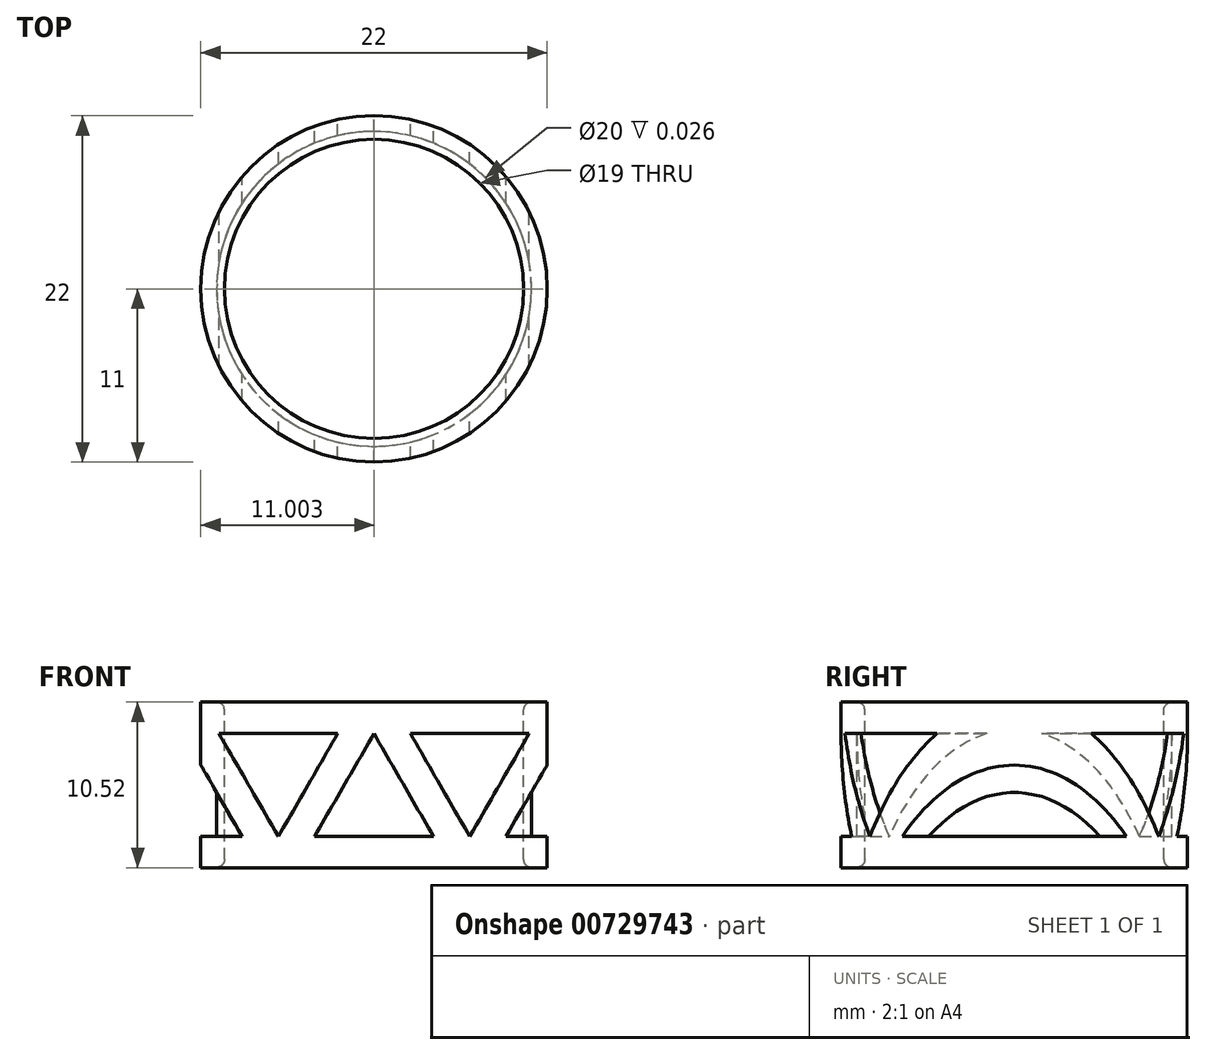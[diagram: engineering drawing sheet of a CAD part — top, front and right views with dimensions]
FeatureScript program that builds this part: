
annotation { "Feature Type Name" : "Feature", "Feature Type Description" : "" }
export const myFeature = defineFeature(function(context is Context, id is Id, definition is map)
    precondition{}
    {
        {
            var Q0;
            Q0=qCreatedBy(makeId("Front.planeOp"),FACE);
            var sketch = newSketch(context, id + "F0", { "sketchPlane" : qUnion([Q0])});
            skLineSegment(sketch, "E0.bottom", {"start": v(-0.17, 7.37) * mm, "end": v(21.83, 7.37) * mm});
            skLineSegment(sketch, "E0.top", {"start": v(-0.17, 17.9) * mm, "end": v(21.83, 17.9) * mm});
            skLineSegment(sketch, "E0.left", {"start": v(-0.17, 7.37) * mm, "end": v(-0.17, 17.9) * mm});
            skLineSegment(sketch, "E0.right", {"start": v(21.83, 7.37) * mm, "end": v(21.83, 17.9) * mm});
            skLineSegment(sketch, "E1", {"start": v(-0.17, 13.9) * mm, "end": v(3.6, 7.37) * mm});
            skLineSegment(sketch, "E2", {"start": v(3.6, 7.37) * mm, "end": v(9.68, 17.9) * mm});
            skLineSegment(sketch, "E3", {"start": v(9.68, 17.9) * mm, "end": v(15.76, 7.37) * mm});
            skLineSegment(sketch, "E4", {"start": v(15.76, 7.37) * mm, "end": v(21.83, 17.9) * mm});
            skLineSegment(sketch, "E5", {"start": v(-0.17, 17.9) * mm, "end": v(5.91, 7.37) * mm});
            skLineSegment(sketch, "E6", {"start": v(5.91, 7.37) * mm, "end": v(11.99, 17.9) * mm});
            skLineSegment(sketch, "E7", {"start": v(11.99, 17.9) * mm, "end": v(18.06, 7.37) * mm});
            skLineSegment(sketch, "E8", {"start": v(18.06, 7.37) * mm, "end": v(21.83, 13.9) * mm});
            skLineSegment(sketch, "E9", {"start": v(-0.17, 15.9) * mm, "end": v(21.83, 15.9) * mm});
            skLineSegment(sketch, "E10", {"start": v(-0.17, 9.37) * mm, "end": v(21.83, 9.37) * mm});
            skSolve(sketch);
        }
        {
            var Q0;
            {var subQ1=sQuery(id+"F0.wireOp",EDGE,"E0.left");var subQ5=sQuery(id+"F0.wireOp",EDGE,"E1");var subQ6=makeQuery(id+"F0.imprint","INTERSECT",VERTEX,{"derivedFrom":[subQ1,subQ5]});Q0=makeQuery(id+"F0.imprint","IMPRINT",FACE,{"disambiguationData":[TD([[makeQuery(id+"F0.imprint","IMPRINT",EDGE,{"disambiguationData":[TD([[subQ6,-1.0]])],"derivedFrom":subQ1}),-1.0]])]});}
            var Q1;
            {var subQ3=sQuery(id+"F0.wireOp",EDGE,"E2");var subQ5=sQuery(id+"F0.wireOp",EDGE,"E9");var subQ6=makeQuery(id+"F0.imprint","INTERSECT",VERTEX,{"derivedFrom":[subQ3,subQ5]});Q1=makeQuery(id+"F0.imprint","IMPRINT",FACE,{"disambiguationData":[TD([[makeQuery(id+"F0.imprint","IMPRINT",EDGE,{"disambiguationData":[TD([[subQ6,1.0]])],"derivedFrom":subQ5}),1.0]])]});}
            var Q2;
            {var subQ1=sQuery(id+"F0.wireOp",EDGE,"E2");var subQ3=sQuery(id+"F0.wireOp",EDGE,"E9");var subQ4=makeQuery(id+"F0.imprint","INTERSECT",VERTEX,{"derivedFrom":[subQ1,subQ3]});Q2=makeQuery(id+"F0.imprint","IMPRINT",FACE,{"disambiguationData":[TD([[makeQuery(id+"F0.imprint","IMPRINT",EDGE,{"disambiguationData":[TD([[subQ4,-1.0]])],"derivedFrom":subQ1}),-1.0]])]});}
            var Q3;
            {var subQ0=sQuery(id+"F0.wireOp",EDGE,"E3");var subQ1=sQuery(id+"F0.wireOp",EDGE,"E0.top");var subQ2=makeQuery(id+"F0.imprint","INTERSECT",VERTEX,{"derivedFrom":[subQ1,sQuery(id+"F0.wireOp",EDGE,"E2"),subQ0]});Q3=makeQuery(id+"F0.imprint","IMPRINT",FACE,{"disambiguationData":[TD([[makeQuery(id+"F0.imprint","IMPRINT",EDGE,{"disambiguationData":[TD([[subQ2,-1.0]])],"derivedFrom":subQ1}),-1.0]])]});}
            var Q4;
            {var subQ0=sQuery(id+"F0.wireOp",EDGE,"E7");var subQ3=sQuery(id+"F0.wireOp",EDGE,"E9");var subQ5=makeQuery(id+"F0.imprint","INTERSECT",VERTEX,{"derivedFrom":[subQ0,subQ3]});Q4=makeQuery(id+"F0.imprint","IMPRINT",FACE,{"disambiguationData":[TD([[makeQuery(id+"F0.imprint","IMPRINT",EDGE,{"disambiguationData":[TD([[subQ5,1.0]])],"derivedFrom":subQ0}),-1.0]])]});}
            var Q5;
            {var subQ1=sQuery(id+"F0.wireOp",EDGE,"E0.left");var subQ3=sQuery(id+"F0.wireOp",EDGE,"E9");var subQ4=makeQuery(id+"F0.imprint","INTERSECT",VERTEX,{"derivedFrom":[subQ1,subQ3]});Q5=makeQuery(id+"F0.imprint","IMPRINT",FACE,{"disambiguationData":[TD([[makeQuery(id+"F0.imprint","IMPRINT",EDGE,{"disambiguationData":[TD([[subQ4,-1.0]])],"derivedFrom":subQ3}),1.0]])]});}
            var Q6;
            {var subQ0=sQuery(id+"F0.wireOp",EDGE,"E4");var subQ5=sQuery(id+"F0.wireOp",EDGE,"E9");var subQ6=makeQuery(id+"F0.imprint","INTERSECT",VERTEX,{"derivedFrom":[subQ0,subQ5]});Q6=makeQuery(id+"F0.imprint","IMPRINT",FACE,{"disambiguationData":[TD([[makeQuery(id+"F0.imprint","IMPRINT",EDGE,{"disambiguationData":[TD([[subQ6,1.0]])],"derivedFrom":subQ5}),1.0]])]});}
            var Q7;
            {var subQ1=sQuery(id+"F0.wireOp",EDGE,"E0.right");var subQ3=sQuery(id+"F0.wireOp",EDGE,"E9");var subQ4=makeQuery(id+"F0.imprint","INTERSECT",VERTEX,{"derivedFrom":[subQ1,subQ3]});Q7=makeQuery(id+"F0.imprint","IMPRINT",FACE,{"disambiguationData":[TD([[makeQuery(id+"F0.imprint","IMPRINT",EDGE,{"disambiguationData":[TD([[subQ4,1.0]])],"derivedFrom":subQ3}),1.0]])]});}
            var Q8;
            {var subQ1=sQuery(id+"F0.wireOp",EDGE,"E0.right");var subQ5=sQuery(id+"F0.wireOp",EDGE,"E8");var subQ6=makeQuery(id+"F0.imprint","INTERSECT",VERTEX,{"derivedFrom":[subQ1,subQ5]});Q8=makeQuery(id+"F0.imprint","IMPRINT",FACE,{"disambiguationData":[TD([[makeQuery(id+"F0.imprint","IMPRINT",EDGE,{"disambiguationData":[TD([[subQ6,-1.0]])],"derivedFrom":subQ1}),1.0]])]});}
            var Q9;
            {var subQ0=sQuery(id+"F0.wireOp",EDGE,"E10");var subQ1=sQuery(id+"F0.wireOp",EDGE,"E3");var subQ2=makeQuery(id+"F0.imprint","INTERSECT",VERTEX,{"derivedFrom":[subQ1,subQ0]});Q9=makeQuery(id+"F0.imprint","IMPRINT",FACE,{"disambiguationData":[TD([[makeQuery(id+"F0.imprint","IMPRINT",EDGE,{"disambiguationData":[TD([[subQ2,1.0]])],"derivedFrom":subQ1}),1.0]])]});}
            var Q10;
            {var subQ0=sQuery(id+"F0.wireOp",EDGE,"E9");var subQ1=sQuery(id+"F0.wireOp",EDGE,"E2");var subQ2=makeQuery(id+"F0.imprint","INTERSECT",VERTEX,{"derivedFrom":[subQ1,subQ0]});Q10=makeQuery(id+"F0.imprint","IMPRINT",FACE,{"disambiguationData":[TD([[makeQuery(id+"F0.imprint","IMPRINT",EDGE,{"disambiguationData":[TD([[subQ2,1.0]])],"derivedFrom":subQ1}),-1.0]])]});}
            var Q11;
            {var subQ0=sQuery(id+"F0.wireOp",EDGE,"E2");var subQ1=sQuery(id+"F0.wireOp",EDGE,"E0.bottom");var subQ2=makeQuery(id+"F0.imprint","INTERSECT",VERTEX,{"derivedFrom":[subQ1,sQuery(id+"F0.wireOp",EDGE,"E1"),subQ0]});Q11=makeQuery(id+"F0.imprint","IMPRINT",FACE,{"disambiguationData":[TD([[makeQuery(id+"F0.imprint","IMPRINT",EDGE,{"disambiguationData":[TD([[subQ2,-1.0]])],"derivedFrom":subQ1}),1.0]])]});}
            var Q12;
            {var subQ1=sQuery(id+"F0.wireOp",EDGE,"E1");var subQ3=sQuery(id+"F0.wireOp",EDGE,"E10");var subQ4=makeQuery(id+"F0.imprint","INTERSECT",VERTEX,{"derivedFrom":[subQ1,subQ3]});Q12=makeQuery(id+"F0.imprint","IMPRINT",FACE,{"disambiguationData":[TD([[makeQuery(id+"F0.imprint","IMPRINT",EDGE,{"disambiguationData":[TD([[subQ4,-1.0]])],"derivedFrom":subQ1}),1.0]])]});}
            var Q13;
            {var subQ0=sQuery(id+"F0.wireOp",EDGE,"E0.left");var subQ1=sQuery(id+"F0.wireOp",EDGE,"E0.bottom");var subQ2=makeQuery(id+"F0.imprint","INTERSECT",VERTEX,{"derivedFrom":[subQ1,subQ0]});Q13=makeQuery(id+"F0.imprint","IMPRINT",FACE,{"disambiguationData":[TD([[makeQuery(id+"F0.imprint","IMPRINT",EDGE,{"disambiguationData":[TD([[subQ2,-1.0]])],"derivedFrom":subQ0}),-1.0]])]});}
            var Q14;
            {var subQ0=sQuery(id+"F0.wireOp",EDGE,"E6");var subQ3=sQuery(id+"F0.wireOp",EDGE,"E10");var subQ5=makeQuery(id+"F0.imprint","INTERSECT",VERTEX,{"derivedFrom":[subQ0,subQ3]});Q14=makeQuery(id+"F0.imprint","IMPRINT",FACE,{"disambiguationData":[TD([[makeQuery(id+"F0.imprint","IMPRINT",EDGE,{"disambiguationData":[TD([[subQ5,1.0]])],"derivedFrom":subQ0}),1.0]])]});}
            var Q15;
            {var subQ0=sQuery(id+"F0.wireOp",EDGE,"E3");var subQ5=sQuery(id+"F0.wireOp",EDGE,"E10");var subQ6=makeQuery(id+"F0.imprint","INTERSECT",VERTEX,{"derivedFrom":[subQ0,subQ5]});Q15=makeQuery(id+"F0.imprint","IMPRINT",FACE,{"disambiguationData":[TD([[makeQuery(id+"F0.imprint","IMPRINT",EDGE,{"disambiguationData":[TD([[subQ6,1.0]])],"derivedFrom":subQ5}),-1.0]])]});}
            var Q16;
            {var subQ1=sQuery(id+"F0.wireOp",EDGE,"E3");var subQ3=sQuery(id+"F0.wireOp",EDGE,"E10");var subQ4=makeQuery(id+"F0.imprint","INTERSECT",VERTEX,{"derivedFrom":[subQ1,subQ3]});Q16=makeQuery(id+"F0.imprint","IMPRINT",FACE,{"disambiguationData":[TD([[makeQuery(id+"F0.imprint","IMPRINT",EDGE,{"disambiguationData":[TD([[subQ4,-1.0]])],"derivedFrom":subQ1}),1.0]])]});}
            var Q17;
            {var subQ0=sQuery(id+"F0.wireOp",EDGE,"E4");var subQ1=sQuery(id+"F0.wireOp",EDGE,"E0.bottom");var subQ2=makeQuery(id+"F0.imprint","INTERSECT",VERTEX,{"derivedFrom":[subQ1,sQuery(id+"F0.wireOp",EDGE,"E3"),subQ0]});Q17=makeQuery(id+"F0.imprint","IMPRINT",FACE,{"disambiguationData":[TD([[makeQuery(id+"F0.imprint","IMPRINT",EDGE,{"disambiguationData":[TD([[subQ2,-1.0]])],"derivedFrom":subQ1}),1.0]])]});}
            var Q18;
            {var subQ0=sQuery(id+"F0.wireOp",EDGE,"E8");var subQ3=sQuery(id+"F0.wireOp",EDGE,"E10");var subQ5=makeQuery(id+"F0.imprint","INTERSECT",VERTEX,{"derivedFrom":[subQ0,subQ3]});Q18=makeQuery(id+"F0.imprint","IMPRINT",FACE,{"disambiguationData":[TD([[makeQuery(id+"F0.imprint","IMPRINT",EDGE,{"disambiguationData":[TD([[subQ5,1.0]])],"derivedFrom":subQ0}),1.0]])]});}
            var Q19;
            {var subQ0=sQuery(id+"F0.wireOp",EDGE,"E0.right");var subQ1=sQuery(id+"F0.wireOp",EDGE,"E0.bottom");var subQ2=makeQuery(id+"F0.imprint","INTERSECT",VERTEX,{"derivedFrom":[subQ1,subQ0]});Q19=makeQuery(id+"F0.imprint","IMPRINT",FACE,{"disambiguationData":[TD([[makeQuery(id+"F0.imprint","IMPRINT",EDGE,{"disambiguationData":[TD([[subQ2,-1.0]])],"derivedFrom":subQ0}),1.0]])]});}
            extrude(context, id + "F1", {"entities" : qUnion([Q0, Q1, Q2, Q3, Q4, Q5, Q6, Q7, Q8, Q9, Q10, Q11, Q12, Q13, Q14, Q15, Q16, Q17, Q18, Q19]), "depth" : 22 * mm, "offsetDistance" : 25 * mm});
        }
        {
            var Q0;
            Q0=makeQuery(id+"F1.opExtrude","SWEPT_FACE",FACE,{"disambiguationData":[OSD([sQuery(id+"F0.wireOp",EDGE,"E0.top")])]});
            var sketch = newSketch(context, id + "F2", { "sketchPlane" : qUnion([Q0])});
            skPoint(sketch, "E11", {"position": v(-0.17, -11) * mm});
            skPoint(sketch, "E12", {"position": v(10.83, 0) * mm});
            skPoint(sketch, "E13", {"position": v(10.83, -11) * mm});
            skCircle(sketch, "E14", {"center": v(10.83, -11) * mm, "radius": 9.5 * mm});
            skCircle(sketch, "E15", {"center": v(10.83, -11) * mm, "radius": 11 * mm});
            skCircle(sketch, "E16", {"center": v(10.83, -11) * mm, "radius": 10 * mm});
            skSolve(sketch);
        }
        {
            var Q0;
            {var subQ0=sQuery(id+"F2.wireOp",EDGE,"E15");var subQ1=sQuery(id+"F0.wireOp",EDGE,"E0.top");var subQ2=makeQuery(id+"F1.opExtrude","CAP_EDGE",EDGE,{"disambiguationData":[OSD([subQ1])],"isStart":true});var subQ3=makeQuery(id+"F2.imprint","INTERSECT",VERTEX,{"derivedFrom":[subQ2,subQ0]});Q0=makeQuery(id+"F2.imprint","IMPRINT",FACE,{"disambiguationData":[TD([[makeQuery(id+"F2.imprint","IMPRINT",EDGE,{"disambiguationData":[TD([[subQ3,-1.0]])],"derivedFrom":subQ0}),-1.0]])]});}
            var Q1;
            {var subQ0=sQuery(id+"F2.wireOp",EDGE,"E15");var subQ1=sQuery(id+"F0.wireOp",EDGE,"E0.top");var subQ2=makeQuery(id+"F1.opExtrude","CAP_EDGE",EDGE,{"disambiguationData":[OSD([subQ1])],"isStart":true});var subQ3=makeQuery(id+"F2.imprint","INTERSECT",VERTEX,{"derivedFrom":[subQ2,subQ0]});Q1=makeQuery(id+"F2.imprint","IMPRINT",FACE,{"disambiguationData":[TD([[makeQuery(id+"F2.imprint","IMPRINT",EDGE,{"disambiguationData":[TD([[subQ3,1.0]])],"derivedFrom":subQ0}),-1.0]])]});}
            var Q2;
            Q2=makeQuery(id+"F2.imprint","IMPRINT",FACE,{"disambiguationData":[TD([[makeQuery(id+"F2.imprint","IMPRINT",EDGE,{"derivedFrom":sQuery(id+"F2.wireOp",EDGE,"E14")}),1.0]])]});
            var Q3;
            {var subQ0=sQuery(id+"F2.wireOp",EDGE,"E15");var subQ1=sQuery(id+"F0.wireOp",EDGE,"E0.top");var subQ4=makeQuery(id+"F1.opExtrude","CAP_EDGE",EDGE,{"disambiguationData":[OSD([subQ1])],"isStart":false});var subQ5=makeQuery(id+"F2.imprint","INTERSECT",VERTEX,{"derivedFrom":[subQ4,subQ0]});Q3=makeQuery(id+"F2.imprint","IMPRINT",FACE,{"disambiguationData":[TD([[makeQuery(id+"F2.imprint","IMPRINT",EDGE,{"disambiguationData":[TD([[subQ5,-1.0]])],"derivedFrom":subQ0}),-1.0]])]});}
            var Q4;
            {var subQ0=sQuery(id+"F2.wireOp",EDGE,"E15");var subQ1=sQuery(id+"F0.wireOp",EDGE,"E0.top");var subQ4=makeQuery(id+"F1.opExtrude","CAP_EDGE",EDGE,{"disambiguationData":[OSD([subQ1])],"isStart":false});var subQ5=makeQuery(id+"F2.imprint","INTERSECT",VERTEX,{"derivedFrom":[subQ4,subQ0]});Q4=makeQuery(id+"F2.imprint","IMPRINT",FACE,{"disambiguationData":[TD([[makeQuery(id+"F2.imprint","IMPRINT",EDGE,{"disambiguationData":[TD([[subQ5,1.0]])],"derivedFrom":subQ0}),-1.0]])]});}
            var Q5;
            Q5=makeQuery(id+"F2.imprint","IMPRINT",FACE,{"disambiguationData":[TD([[makeQuery(id+"F2.imprint","IMPRINT",EDGE,{"derivedFrom":sQuery(id+"F2.wireOp",EDGE,"E14")}),-1.0]])]});
            extrude(context, id + "F3", {"entities" : qUnion([Q0, Q1, Q2, Q3, Q4, Q5]), "operationType" : NewBodyOperationType.REMOVE, "oppositeDirection" : true, "depth" : 25 * mm, "offsetDistance" : 25 * mm});
        }
        {
            var Q0;
            Q0=makeQuery(id+"F2.imprint","IMPRINT",FACE,{"disambiguationData":[TD([[makeQuery(id+"F2.imprint","IMPRINT",EDGE,{"derivedFrom":sQuery(id+"F2.wireOp",EDGE,"E14")}),-1.0]])]});
            extrude(context, id + "F4", {"entities" : qUnion([Q0]), "operationType" : NewBodyOperationType.ADD, "oppositeDirection" : true, "depth" : 10.5 * mm, "offsetDistance" : 25 * mm});
        }
        {
            var Q0;
            Q0=makeQuery(id+"F4.opExtrude","CAP_EDGE",EDGE,{"disambiguationData":[OSD([sQuery(id+"F2.wireOp",EDGE,"E14")])],"isStart":false});
            var Q1;
            Q1=makeQuery(id+"F4.opExtrude","CAP_EDGE",EDGE,{"disambiguationData":[OSD([sQuery(id+"F2.wireOp",EDGE,"E14")])],"isStart":true});
            fillet(context, id + "F5", {"entities" : qUnion([Q0, Q1]), "radius" : .5 * mm, "tangentPropagation" : true, "allowEdgeOverflow" : false});
        }
    });
